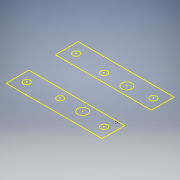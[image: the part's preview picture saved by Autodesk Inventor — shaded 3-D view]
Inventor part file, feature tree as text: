
AUTODESK INVENTOR PART (.ipt)
format: ipt  version: 2016 SP1 (Build 200210100, 210)  size: 118,272 bytes
history: native  units: mm
features: reference x2, extrude x1, sketch x1
ambient origin geometry x8: Origin, YZ Plane, XZ Plane, XY Plane, X Axis, Y Axis, Z Axis, Center Point
bodies: Solid1 (feature_tree)
feature tree (4):
  extrude  "Extrusion1"  Depth=160.0mm
  sketch  "Sketch1"  dims[d0=100.0mm d1=160.0mm d2=20.0mm d3=10.0mm d4=72.0mm d5=0.0mm d6=80.0mm d7=5.0mm d8=5.0mm d9=6.0mm d10=6.0mm d11=8.0mm d12=0.0mm]
  reference  "Reference1"
  reference  "Reference2"
